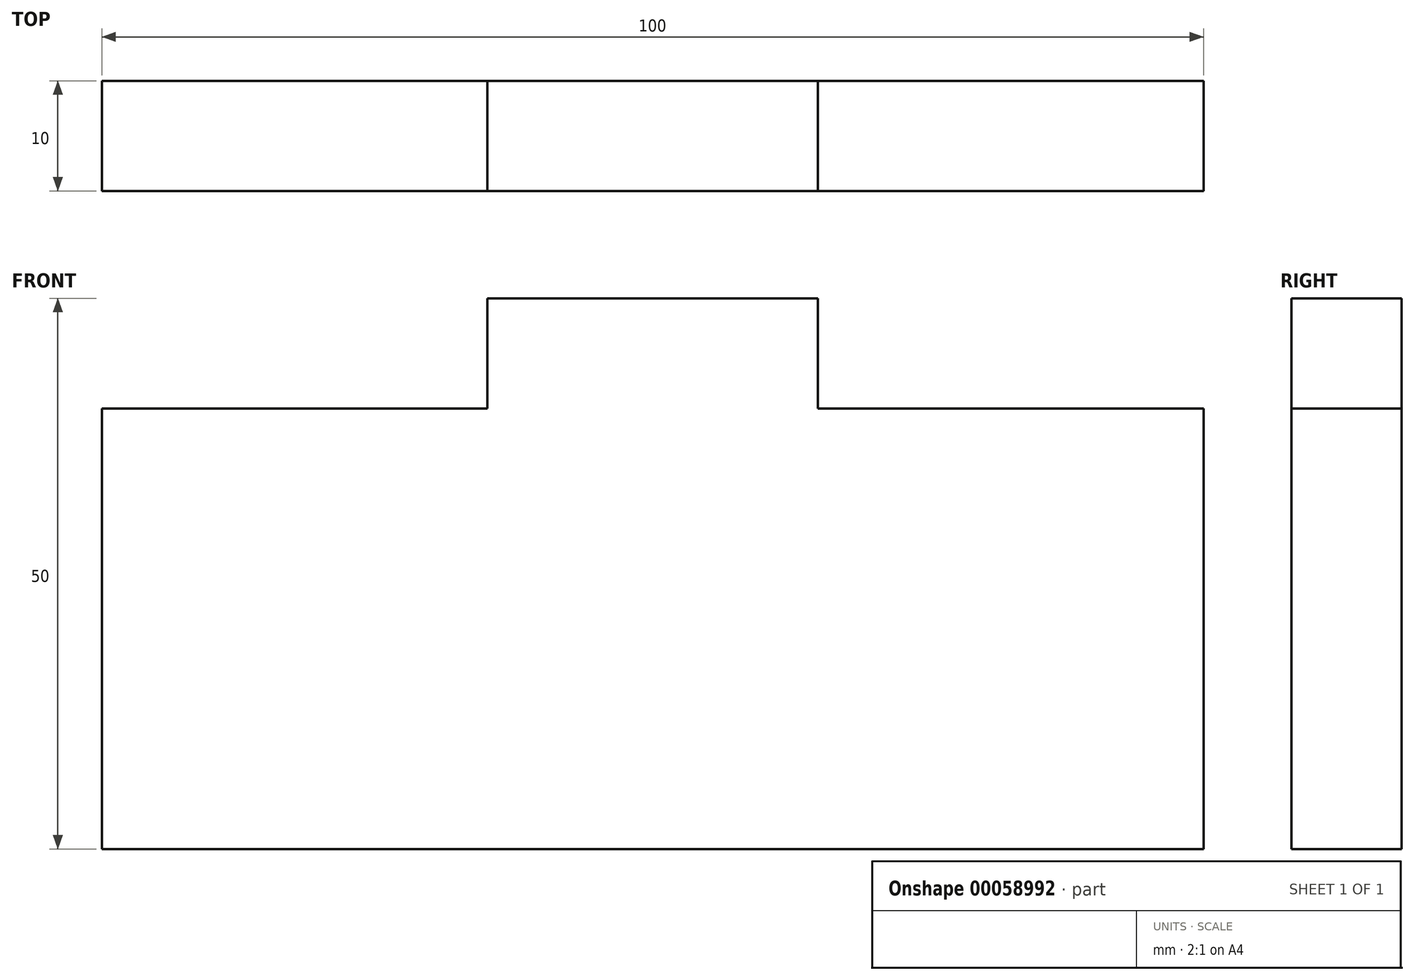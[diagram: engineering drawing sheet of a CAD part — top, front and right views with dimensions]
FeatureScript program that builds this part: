
annotation { "Feature Type Name" : "Feature", "Feature Type Description" : "" }
export const myFeature = defineFeature(function(context is Context, id is Id, definition is map)
    precondition{}
    {
        {
            var Q0;
            Q0=qCreatedBy(makeId("Front.planeOp"),FACE);
            var sketch = newSketch(context, id + "F0", { "sketchPlane" : qUnion([Q0])});
            skLineSegment(sketch, "E0.bottom", {"start": v(-50, 20) * mm, "end": v(50, 20) * mm});
            skLineSegment(sketch, "E0.top", {"start": v(-50, -20) * mm, "end": v(50, -20) * mm});
            skLineSegment(sketch, "E0.left", {"start": v(-50, 20) * mm, "end": v(-50, -20) * mm});
            skLineSegment(sketch, "E0.right", {"start": v(50, 20) * mm, "end": v(50, -20) * mm});
            skPoint(sketch, "E0.middle", {"position": v(0, 0) * mm});
            skSolve(sketch);
        }
        {
            var Q0;
            Q0 = qSketchRegion(id + "F0", true);
            extrude(context, id + "F1", {"entities" : qUnion([Q0]), "depth" : 10 * mm});
        }
        {
            var Q0;
            Q0=makeQuery(id+"F1.opExtrude","SWEPT_FACE",FACE,{"disambiguationData":[OSD([sQuery(id+"F0.wireOp",EDGE,"E0.bottom")])]});
            var sketch = newSketch(context, id + "F2", { "sketchPlane" : qUnion([Q0])});
            skLineSegment(sketch, "E1", {"start": v(-50, -5) * mm, "end": v(50, -5) * mm, "construction": true});
            skLineSegment(sketch, "E2.bottom", {"start": v(-15, 0) * mm, "end": v(15, 0) * mm});
            skLineSegment(sketch, "E2.top", {"start": v(-15, -10) * mm, "end": v(15, -10) * mm});
            skLineSegment(sketch, "E2.left", {"start": v(-15, 0) * mm, "end": v(-15, -10) * mm});
            skLineSegment(sketch, "E2.right", {"start": v(15, 0) * mm, "end": v(15, -10) * mm});
            skPoint(sketch, "E2.middle", {"position": v(0, -5) * mm});
            skSolve(sketch);
        }
        {
            var Q0;
            Q0 = qSketchRegion(id + "F2", true);
            extrude(context, id + "F3", {"entities" : qUnion([Q0]), "operationType" : NewBodyOperationType.ADD, "depth" : 10 * mm});
        }
    });
